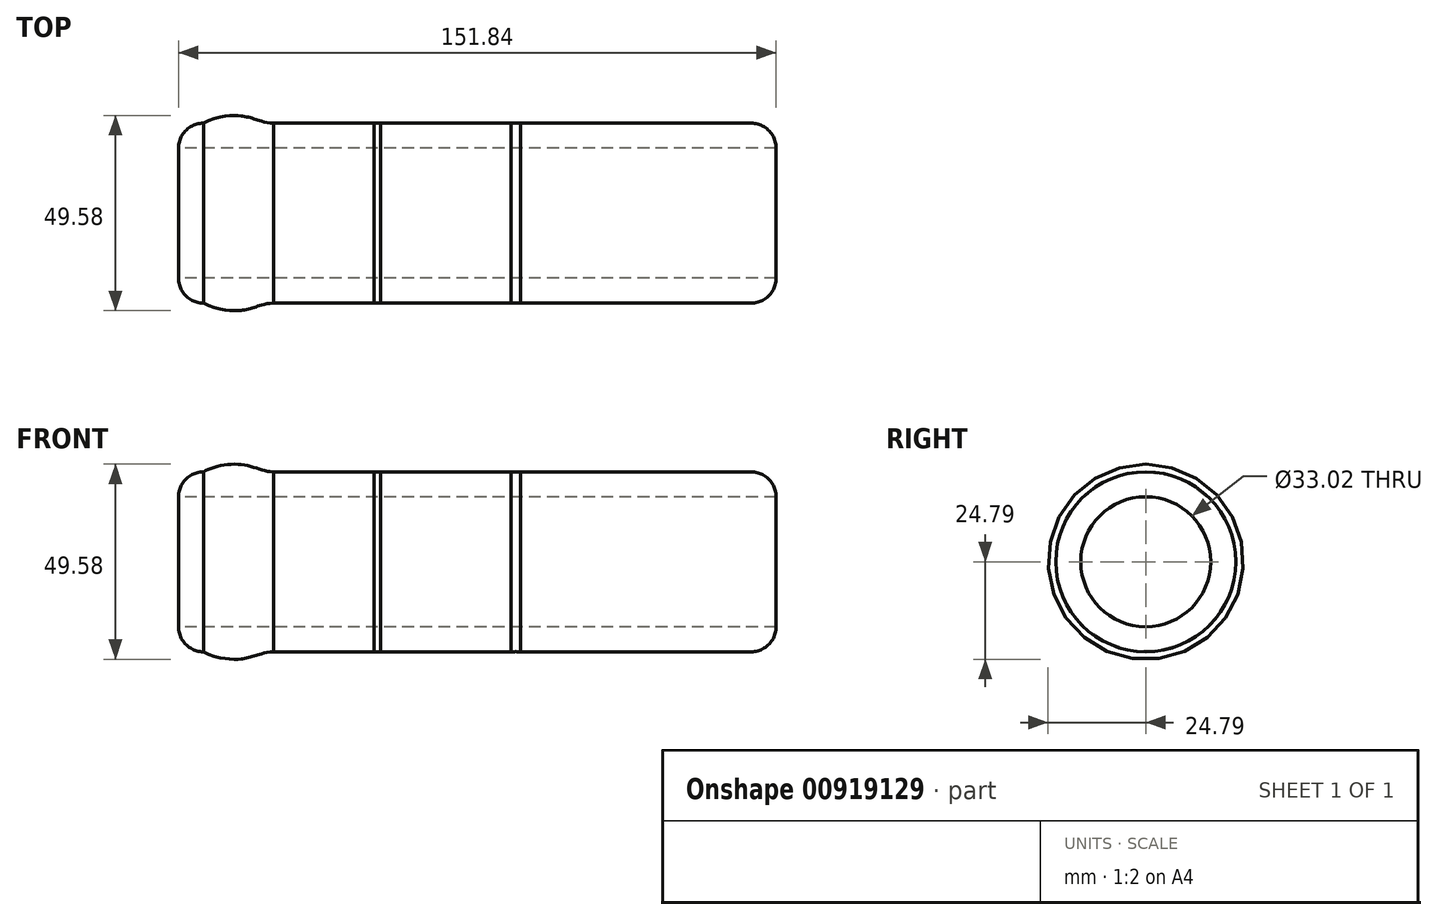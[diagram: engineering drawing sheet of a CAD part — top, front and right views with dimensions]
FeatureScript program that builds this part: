
annotation { "Feature Type Name" : "Feature", "Feature Type Description" : "" }
export const myFeature = defineFeature(function(context is Context, id is Id, definition is map)
    precondition{}
    {
        {
            var Q0;
            Q0=qCreatedBy(makeId("Front.planeOp"),FACE);
            var sketch = newSketch(context, id + "F0", { "sketchPlane" : qUnion([Q0])});
            skLineSegment(sketch, "E0", {"start": v(0, 0) * mm, "end": v(76.2, 0) * mm, "construction": true});
            skLineSegment(sketch, "E1", {"start": v(76.2, 0) * mm, "end": v(76.2, 16.51) * mm, "construction": true});
            skLineSegment(sketch, "E2.bottom", {"start": v(76.2, 16.51) * mm, "end": v(-75.64, 16.51) * mm});
            skLineSegment(sketch, "E2.top", {"start": v(69.85, 22.86) * mm, "end": v(-69.3, 22.86) * mm});
            skLineSegment(sketch, "E2.left", {"start": v(76.2, 16.51) * mm, "end": v(76.2, 16.5) * mm});
            skLineSegment(sketch, "E2.right", {"start": v(-75.64, 16.5) * mm, "end": v(-75.64, 16.5) * mm});
            skPoint(sketch, "E3.visualSharp", {"position": v(-75.64, 22.86) * mm});
            skArc(sketch, "E3.filletArc", {"start": v(-69.3, 22.86) * mm, "mid": v(-73.78, 21) * mm, "end": v(-75.64, 16.5) * mm});
            skPoint(sketch, "E4.visualSharp", {"position": v(76.2, 22.86) * mm});
            skArc(sketch, "E4.filletArc", {"start": v(76.2, 16.5) * mm, "mid": v(74.34, 21) * mm, "end": v(69.85, 22.86) * mm});
            skFitSpline(sketch, "E5", {"points": [v(-69.3, 22.86) * mm, v(-59.61, 24.7) * mm, v(-51.42, 22.86) * mm, v(-41.51, 25.04) * mm, v(-25.97, 22.86) * mm, v(-9.58, 24.7) * mm, v(11.25, 22.86) * mm, v(32.43, 25.72) * mm, v(50.7, 22.86) * mm, v(64.36, 24.86) * mm, v(69.85, 22.86) * mm], "startDerivative": vector(77.65, 46.4) * mm, "endDerivative": vector(71.75, -43.35) * mm});
            skSolve(sketch);
        }
        {
            var Q0;
            {var subQ0=sQuery(id+"F0.wireOp",EDGE,"E5");var subQ1=sQuery(id+"F0.wireOp",EDGE,"E2.top");var subQ2=makeQuery(id+"F0.imprint","INTERSECT",VERTEX,{"disambiguationData":[OD(5.0)],"derivedFrom":[subQ1,subQ0]});Q0=makeQuery(id+"F0.imprint","IMPRINT",FACE,{"disambiguationData":[TD([[makeQuery(id+"F0.imprint","IMPRINT",EDGE,{"disambiguationData":[TD([[subQ2,-1.0]])],"derivedFrom":subQ1}),-1.0]])]});}
            var Q1;
            Q1=makeQuery(id+"F0.imprint","IMPRINT",FACE,{"disambiguationData":[TD([[makeQuery(id+"F0.imprint","IMPRINT",EDGE,{"derivedFrom":sQuery(id+"F0.wireOp",EDGE,"E2.bottom")}),-1.0]])]});
            var Q2;
            {var subQ0=sQuery(id+"F0.wireOp",EDGE,"E5");var subQ1=sQuery(id+"F0.wireOp",EDGE,"E2.top");var subQ2=makeQuery(id+"F0.imprint","INTERSECT",VERTEX,{"disambiguationData":[OD(3.0)],"derivedFrom":[subQ1,subQ0]});Q2=makeQuery(id+"F0.imprint","IMPRINT",FACE,{"disambiguationData":[TD([[makeQuery(id+"F0.imprint","IMPRINT",EDGE,{"disambiguationData":[TD([[subQ2,-1.0]])],"derivedFrom":subQ1}),-1.0]])]});}
            var Q3;
            {var subQ0=sQuery(id+"F0.wireOp",EDGE,"E5");var subQ1=sQuery(id+"F0.wireOp",EDGE,"E2.top");var subQ2=makeQuery(id+"F0.imprint","INTERSECT",VERTEX,{"disambiguationData":[OD(1.0)],"derivedFrom":[subQ1,subQ0]});Q3=makeQuery(id+"F0.imprint","IMPRINT",FACE,{"disambiguationData":[TD([[makeQuery(id+"F0.imprint","IMPRINT",EDGE,{"disambiguationData":[TD([[subQ2,-1.0]])],"derivedFrom":subQ1}),-1.0]])]});}
            var Q4;
            {var subQ0=sQuery(id+"F0.wireOp",EDGE,"E5");var subQ1=sQuery(id+"F0.wireOp",EDGE,"E2.top");var subQ3=makeQuery(id+"F0.imprint","INTERSECT",VERTEX,{"disambiguationData":[OD(0.0)],"derivedFrom":[subQ1,subQ0]});Q4=makeQuery(id+"F0.imprint","IMPRINT",FACE,{"disambiguationData":[TD([[makeQuery(id+"F0.imprint","IMPRINT",EDGE,{"disambiguationData":[TD([[subQ3,1.0]])],"derivedFrom":subQ1}),-1.0]])]});}
            var Q5;
            {var subQ0=sQuery(id+"F0.wireOp",EDGE,"E5");var subQ1=sQuery(id+"F0.wireOp",EDGE,"E2.top");var subQ3=makeQuery(id+"F0.imprint","INTERSECT",VERTEX,{"disambiguationData":[OD(7.0)],"derivedFrom":[subQ1,subQ0]});Q5=makeQuery(id+"F0.imprint","IMPRINT",FACE,{"disambiguationData":[TD([[makeQuery(id+"F0.imprint","IMPRINT",EDGE,{"disambiguationData":[TD([[subQ3,-1.0]])],"derivedFrom":subQ1}),-1.0]])]});}
            var Q6;
            Q6=sQuery(id+"F0.wireOp",EDGE,"E0");
            revolve(context, id + "F1", {"surfaceOperationType" : NewSurfaceOperationType.NEW, "entities" : qUnion([Q0, Q1, Q2, Q3, Q4, Q5]), "axis" : qUnion([Q6]), "revolveType" : RevolveType.FULL});
        }
    });
